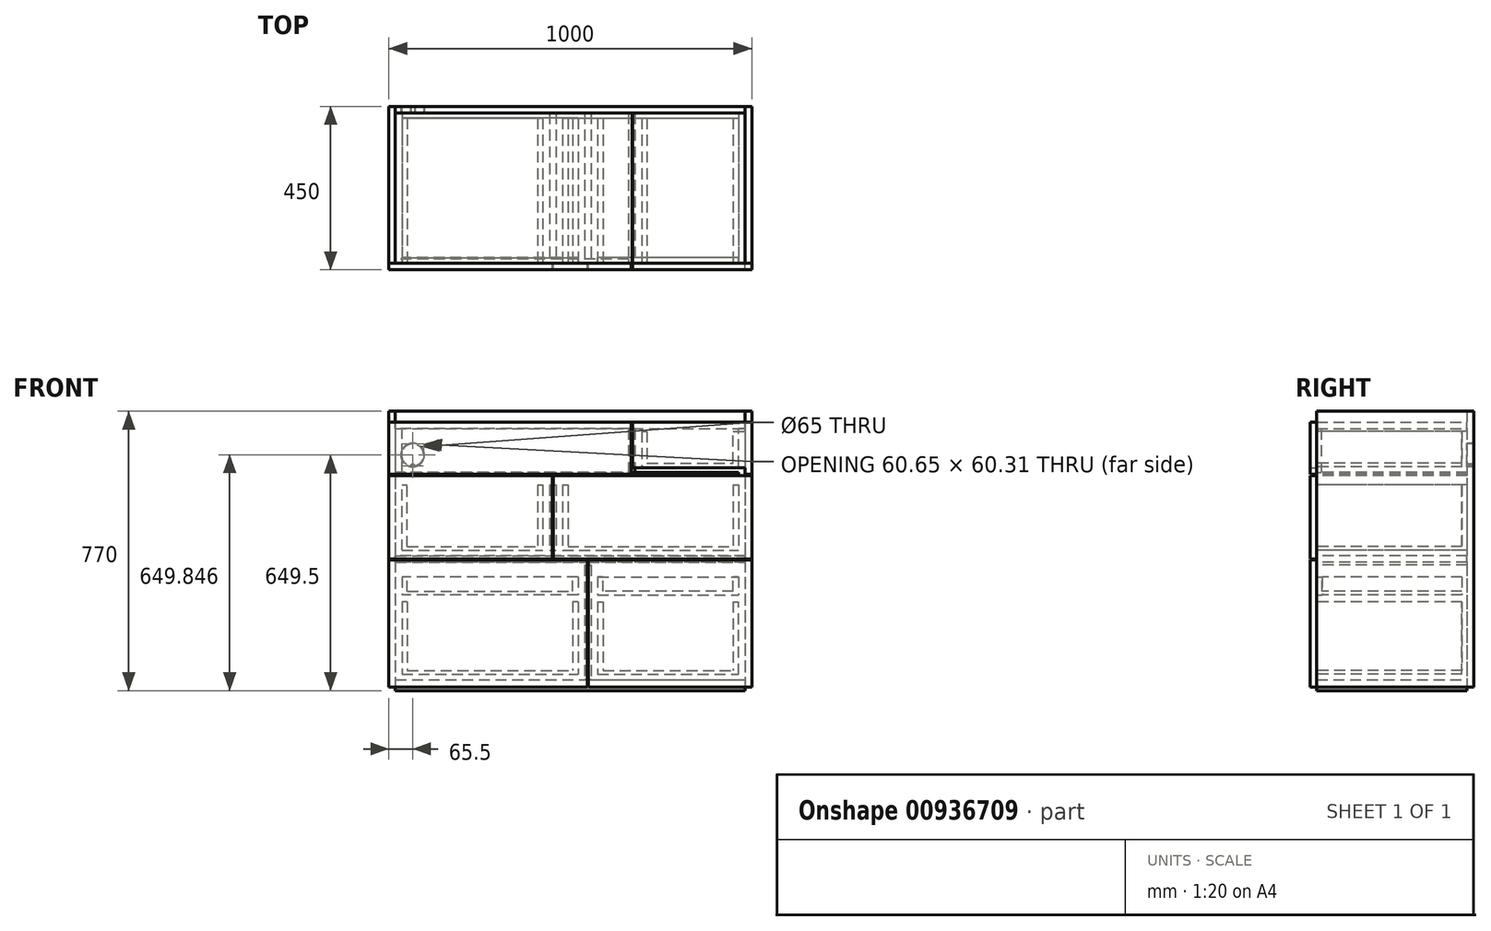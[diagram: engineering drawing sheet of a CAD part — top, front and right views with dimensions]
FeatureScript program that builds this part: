
annotation { "Feature Type Name" : "Feature", "Feature Type Description" : "" }
export const myFeature = defineFeature(function(context is Context, id is Id, definition is map)
    precondition{}
    {
        {
            var Q0;
            Q0=qCreatedBy(makeId("Top.planeOp"),FACE);
            var sketch = newSketch(context, id + "F0", { "sketchPlane" : qUnion([Q0])});
            skLineSegment(sketch, "E0.bottom", {"start": v(0, 0) * mm, "end": v(1000, 0) * mm});
            skLineSegment(sketch, "E0.top", {"start": v(0, 432) * mm, "end": v(1000, 432) * mm});
            skLineSegment(sketch, "E0.left", {"start": v(0, 0) * mm, "end": v(0, 432) * mm});
            skLineSegment(sketch, "E0.right", {"start": v(1000, 0) * mm, "end": v(1000, 432) * mm});
            skLineSegment(sketch, "E1.0", {"start": v(18, 0) * mm, "end": v(18, 432) * mm});
            skLineSegment(sketch, "E2", {"start": v(500, 455.77) * mm, "end": v(500, 504.04) * mm, "construction": true});
            skPoint(sketch, "E2.startSnap0", {"position": v(500, 432) * mm});
            skLineSegment(sketch, "E3.MirrorCS", {"start": v(982, 0) * mm, "end": v(982, 432) * mm});
            skLineSegment(sketch, "E4", {"start": v(1025.2, 216) * mm, "end": v(1096.23, 216) * mm, "construction": true});
            skPoint(sketch, "E4.startSnap0", {"position": v(1000, 216) * mm});
            skLineSegment(sketch, "E5.0", {"start": v(0, 414) * mm, "end": v(1000, 414) * mm});
            skSolve(sketch);
        }
        {
            var Q0;
            {var subQ0=sQuery(id+"F0.wireOp",EDGE,"E0.left");var subQ1=sQuery(id+"F0.wireOp",EDGE,"E0.bottom");var subQ2=makeQuery(id+"F0.imprint","INTERSECT",VERTEX,{"derivedFrom":[subQ1,subQ0]});Q0=makeQuery(id+"F0.imprint","IMPRINT",FACE,{"disambiguationData":[TD([[makeQuery(id+"F0.imprint","IMPRINT",EDGE,{"disambiguationData":[TD([[subQ2,-1.0]])],"derivedFrom":subQ1}),1.0]])]});}
            var Q1;
            {var subQ0=sQuery(id+"F0.wireOp",EDGE,"E0.left");var subQ1=sQuery(id+"F0.wireOp",EDGE,"E0.top");var subQ2=makeQuery(id+"F0.imprint","INTERSECT",VERTEX,{"derivedFrom":[subQ1,subQ0]});Q1=makeQuery(id+"F0.imprint","IMPRINT",FACE,{"disambiguationData":[TD([[makeQuery(id+"F0.imprint","IMPRINT",EDGE,{"disambiguationData":[TD([[subQ2,-1.0]])],"derivedFrom":subQ1}),-1.0]])]});}
            var Q2;
            {var subQ0=sQuery(id+"F0.wireOp",EDGE,"E0.right");var subQ1=sQuery(id+"F0.wireOp",EDGE,"E0.bottom");var subQ2=makeQuery(id+"F0.imprint","INTERSECT",VERTEX,{"derivedFrom":[subQ1,subQ0]});Q2=makeQuery(id+"F0.imprint","IMPRINT",FACE,{"disambiguationData":[TD([[makeQuery(id+"F0.imprint","IMPRINT",EDGE,{"disambiguationData":[TD([[subQ2,1.0]])],"derivedFrom":subQ1}),1.0]])]});}
            var Q3;
            {var subQ0=sQuery(id+"F0.wireOp",EDGE,"E0.right");var subQ1=sQuery(id+"F0.wireOp",EDGE,"E0.top");var subQ2=makeQuery(id+"F0.imprint","INTERSECT",VERTEX,{"derivedFrom":[subQ1,subQ0]});Q3=makeQuery(id+"F0.imprint","IMPRINT",FACE,{"disambiguationData":[TD([[makeQuery(id+"F0.imprint","IMPRINT",EDGE,{"disambiguationData":[TD([[subQ2,1.0]])],"derivedFrom":subQ1}),-1.0]])]});}
            extrude(context, id + "F1", {"entities" : qUnion([Q0, Q1, Q2, Q3]), "depth" : 760 * mm, "offsetDistance" : 25 * mm});
        }
        {
            var Q0;
            {var subQ0=sQuery(id+"F0.wireOp",EDGE,"E1.0");var subQ1=sQuery(id+"F0.wireOp",EDGE,"E0.top");var subQ2=makeQuery(id+"F0.imprint","INTERSECT",VERTEX,{"derivedFrom":[subQ1,subQ0]});Q0=makeQuery(id+"F0.imprint","IMPRINT",FACE,{"disambiguationData":[TD([[makeQuery(id+"F0.imprint","IMPRINT",EDGE,{"disambiguationData":[TD([[subQ2,-1.0]])],"derivedFrom":subQ1}),-1.0]])]});}
            var Q1;
            Q1=makeQuery(id+"F1.opExtrude","CAP_FACE",FACE,{"disambiguationData":[OSD([sQuery(id+"F0.wireOp",EDGE,"E0.bottom"),sQuery(id+"F0.wireOp",EDGE,"E0.top"),sQuery(id+"F0.wireOp",EDGE,"E0.left"),sQuery(id+"F0.wireOp",EDGE,"E1.0")])],"isStart":false});
            extrude(context, id + "F2", {"entities" : qUnion([Q0]), "endBound" : BoundingType.UP_TO_SURFACE, "depth" : 25 * mm, "endBoundEntityFace" : qUnion([Q1]), "offsetDistance" : 25 * mm});
        }
        {
            var Q0;
            {var subQ0=sQuery(id+"F0.wireOp",EDGE,"E1.0");var subQ1=sQuery(id+"F0.wireOp",EDGE,"E0.bottom");var subQ2=makeQuery(id+"F0.imprint","INTERSECT",VERTEX,{"derivedFrom":[subQ1,subQ0]});Q0=makeQuery(id+"F0.imprint","IMPRINT",FACE,{"disambiguationData":[TD([[makeQuery(id+"F0.imprint","IMPRINT",EDGE,{"disambiguationData":[TD([[subQ2,-1.0]])],"derivedFrom":subQ1}),1.0]])]});}
            extrude(context, id + "F3", {"entities" : qUnion([Q0]), "depth" : 20 * mm, "offsetDistance" : 25 * mm, "hasSecondDirection" : true, "secondDirectionOppositeDirection" : true, "secondDirectionDepth" : 10 * mm});
        }
        {
            var Q0;
            Q0=makeQuery(id+"F1.opExtrude","CAP_FACE",FACE,{"disambiguationData":[OSD([sQuery(id+"F0.wireOp",EDGE,"E0.bottom"),sQuery(id+"F0.wireOp",EDGE,"E0.top"),sQuery(id+"F0.wireOp",EDGE,"E0.left"),sQuery(id+"F0.wireOp",EDGE,"E1.0")])],"isStart":false});
            var sketch = newSketch(context, id + "F4", { "sketchPlane" : qUnion([Q0])});
            skLineSegment(sketch, "E6.bottom", {"start": v(0, 432) * mm, "end": v(1000, 432) * mm});
            skLineSegment(sketch, "E6.top", {"start": v(0, 0) * mm, "end": v(1000, 0) * mm});
            skLineSegment(sketch, "E6.left", {"start": v(0, 432) * mm, "end": v(0, 0) * mm});
            skLineSegment(sketch, "E6.right", {"start": v(1000, 432) * mm, "end": v(1000, 0) * mm});
            skLineSegment(sketch, "E7.bottom", {"start": v(18, 0) * mm, "end": v(982, 0) * mm});
            skLineSegment(sketch, "E7.top", {"start": v(18, 414) * mm, "end": v(982, 414) * mm});
            skLineSegment(sketch, "E7.left", {"start": v(18, 0) * mm, "end": v(18, 414) * mm});
            skLineSegment(sketch, "E7.right", {"start": v(982, 0) * mm, "end": v(982, 414) * mm});
            skLineSegment(sketch, "E8", {"start": v(671, 414) * mm, "end": v(671, 0) * mm});
            skLineSegment(sketch, "E9", {"start": v(18, 300) * mm, "end": v(671, 300) * mm});
            skLineSegment(sketch, "E10", {"start": v(55.2, 414) * mm, "end": v(55.2, -186) * mm, "construction": true});
            skLineSegment(sketch, "E11", {"start": v(-81.86, 114) * mm, "end": v(55.2, 114) * mm, "construction": true});
            skLineSegment(sketch, "E12", {"start": v(55.2, 0) * mm, "end": v(-78.13, 0) * mm, "construction": true});
            skLineSegment(sketch, "E13", {"start": v(55.2, -186) * mm, "end": v(-68.9, -186) * mm, "construction": true});
            skLineSegment(sketch, "E14.0", {"start": v(670, 414) * mm, "end": v(670, 0) * mm});
            skSolve(sketch);
        }
        {
            var Q0;
            {var subQ0=sQuery(id+"F4.wireOp",EDGE,"E7.right");Q0=makeQuery(id+"F4.imprint","IMPRINT",FACE,{"disambiguationData":[TD([[makeQuery(id+"F4.imprint","IMPRINT",EDGE,{"derivedFrom":subQ0}),1.0]])]});}
            var Q1;
            {var subQ0=sQuery(id+"F4.wireOp",EDGE,"E7.left");var subQ5=sQuery(id+"F4.wireOp",EDGE,"E9");var subQ7=makeQuery(id+"F4.imprint","INTERSECT",VERTEX,{"derivedFrom":[subQ0,subQ5]});Q1=makeQuery(id+"F4.imprint","IMPRINT",FACE,{"disambiguationData":[TD([[makeQuery(id+"F4.imprint","IMPRINT",EDGE,{"disambiguationData":[TD([[subQ7,-1.0]])],"derivedFrom":subQ5}),1.0]])]});}
            var Q2;
            {var subQ0=sQuery(id+"F4.wireOp",EDGE,"E7.left");var subQ5=sQuery(id+"F4.wireOp",EDGE,"E9");var subQ6=makeQuery(id+"F4.imprint","INTERSECT",VERTEX,{"derivedFrom":[subQ0,subQ5]});Q2=makeQuery(id+"F4.imprint","IMPRINT",FACE,{"disambiguationData":[TD([[makeQuery(id+"F4.imprint","IMPRINT",EDGE,{"disambiguationData":[TD([[subQ6,-1.0]])],"derivedFrom":subQ5}),-1.0]])]});}
            extrude(context, id + "F5", {"entities" : qUnion([Q0, Q1, Q2]), "oppositeDirection" : true, "depth" : 18 * mm, "offsetDistance" : 25 * mm});
        }
        {
            var Q0;
            Q0=makeQuery(id+"FaU98XOoRjI6tdl_2.opExtrude","SWEPT_BODY",BODY,{"disambiguationData":[OSD([sQuery(id+"F4.wireOp",EDGE,"E7.bottom"),sQuery(id+"F4.wireOp",EDGE,"E7.top"),sQuery(id+"F4.wireOp",EDGE,"E7.left"),sQuery(id+"F4.wireOp",EDGE,"E8")])]});
            var Q1;
            Q1=makeQuery(id+"F5.opExtrude","SWEPT_BODY",BODY,{"disambiguationData":[OSD([sQuery(id+"F4.wireOp",EDGE,"E7.bottom"),sQuery(id+"F4.wireOp",EDGE,"E7.top"),sQuery(id+"F4.wireOp",EDGE,"E7.right"),sQuery(id+"F4.wireOp",EDGE,"E8")])]});
            var Q2;
            Q2=makeQuery(id+"F5.opExtrude","SWEPT_BODY",BODY,{"disambiguationData":[OSD([sQuery(id+"F4.wireOp",EDGE,"E7.bottom"),sQuery(id+"F4.wireOp",EDGE,"E7.top"),sQuery(id+"F4.wireOp",EDGE,"E7.left"),sQuery(id+"F4.wireOp",EDGE,"E14.0")])]});
            transform(context, id + "F6", {"entities" : qUnion([Q0, Q1, Q2]), "transformType" : TransformType.TRANSLATION_3D, "dx" : 0 * mm, "dy" : 0 * mm, "dz" : -30 * mm, "makeCopy" : false});
        }
        {
            var Q0;
            {var subQ0=sQuery(id+"F0.wireOp",EDGE,"E0.bottom");Q0=makeQuery(id+"F1.opExtrude","SWEPT_FACE",FACE,{"disambiguationData":[OSD([subQ0]),TDD([makeQuery(id+"F0.imprint","IMPRINT",EDGE,{"disambiguationData":[TD([[makeQuery(id+"F0.imprint","INTERSECT",VERTEX,{"derivedFrom":[subQ0,sQuery(id+"F0.wireOp",EDGE,"E0.left")]}),-1.0]])],"derivedFrom":subQ0})])]});}
            var sketch = newSketch(context, id + "F7", { "sketchPlane" : qUnion([Q0])});
            skLineSegment(sketch, "E15.bottom", {"start": v(0, 730) * mm, "end": v(668, 730) * mm});
            skLineSegment(sketch, "E15.top", {"start": v(0, 586) * mm, "end": v(668, 586) * mm});
            skLineSegment(sketch, "E15.left", {"start": v(0, 730) * mm, "end": v(0, 586) * mm});
            skLineSegment(sketch, "E15.right", {"start": v(668, 730) * mm, "end": v(668, 586) * mm});
            skLineSegment(sketch, "E16.bottom", {"start": v(1000, 583) * mm, "end": v(756, 583) * mm});
            skLineSegment(sketch, "E16.top", {"start": v(1000, 353) * mm, "end": v(756, 353) * mm});
            skLineSegment(sketch, "E16.left", {"start": v(1000, 583) * mm, "end": v(1000, 353) * mm});
            skLineSegment(sketch, "E16.right", {"start": v(756, 583) * mm, "end": v(756, 353) * mm});
            skLineSegment(sketch, "E17.bottom", {"start": v(753, 583) * mm, "end": v(453, 583) * mm});
            skLineSegment(sketch, "E17.top", {"start": v(753, 353) * mm, "end": v(453, 353) * mm});
            skLineSegment(sketch, "E17.left", {"start": v(753, 583) * mm, "end": v(753, 353) * mm});
            skLineSegment(sketch, "E17.right", {"start": v(453, 583) * mm, "end": v(453, 353) * mm});
            skLineSegment(sketch, "E18.bottom", {"start": v(450, 583) * mm, "end": v(0, 583) * mm});
            skLineSegment(sketch, "E18.top", {"start": v(450, 353) * mm, "end": v(0, 353) * mm});
            skLineSegment(sketch, "E18.left", {"start": v(450, 583) * mm, "end": v(450, 353) * mm});
            skLineSegment(sketch, "E18.right", {"start": v(0, 583) * mm, "end": v(0, 353) * mm});
            skLineSegment(sketch, "E19.bottom", {"start": v(671, 730) * mm, "end": v(1000, 730) * mm});
            skLineSegment(sketch, "E19.top", {"start": v(671, 586) * mm, "end": v(1000, 586) * mm});
            skLineSegment(sketch, "E19.left", {"start": v(671, 730) * mm, "end": v(671, 586) * mm});
            skLineSegment(sketch, "E19.right", {"start": v(1000, 730) * mm, "end": v(1000, 586) * mm});
            skLineSegment(sketch, "E20", {"start": v(668, 658) * mm, "end": v(671, 658) * mm, "construction": true});
            skLineSegment(sketch, "E21", {"start": v(1108.22, 586) * mm, "end": v(1108.22, 583) * mm, "construction": true});
            skLineSegment(sketch, "E22", {"start": v(756, 468) * mm, "end": v(753, 468) * mm, "construction": true});
            skLineSegment(sketch, "E23", {"start": v(453, 468) * mm, "end": v(450, 468) * mm, "construction": true});
            skLineSegment(sketch, "E24.bottom", {"start": v(0, 0) * mm, "end": v(244, 0) * mm});
            skLineSegment(sketch, "E24.top", {"start": v(0, 350) * mm, "end": v(244, 350) * mm});
            skLineSegment(sketch, "E24.left", {"start": v(0, 0) * mm, "end": v(0, 350) * mm});
            skLineSegment(sketch, "E24.right", {"start": v(244, 0) * mm, "end": v(244, 350) * mm});
            skLineSegment(sketch, "E25.bottom", {"start": v(247, 350) * mm, "end": v(547, 350) * mm});
            skLineSegment(sketch, "E25.top", {"start": v(247, 0) * mm, "end": v(547, 0) * mm});
            skLineSegment(sketch, "E25.left", {"start": v(247, 350) * mm, "end": v(247, 0) * mm});
            skLineSegment(sketch, "E25.right", {"start": v(547, 350) * mm, "end": v(547, 0) * mm});
            skLineSegment(sketch, "E26.bottom", {"start": v(550, 350) * mm, "end": v(1000, 350) * mm});
            skLineSegment(sketch, "E26.top", {"start": v(550, 0) * mm, "end": v(1000, 0) * mm});
            skLineSegment(sketch, "E26.left", {"start": v(550, 350) * mm, "end": v(550, 0) * mm});
            skLineSegment(sketch, "E26.right", {"start": v(1000, 350) * mm, "end": v(1000, 0) * mm});
            skLineSegment(sketch, "E27", {"start": v(122, 353) * mm, "end": v(122, 350) * mm, "construction": true});
            skPoint(sketch, "E27.startSnap0", {"position": v(122, 350) * mm});
            skLineSegment(sketch, "E28", {"start": v(244, 175) * mm, "end": v(247, 175) * mm, "construction": true});
            skLineSegment(sketch, "E29", {"start": v(550, 175) * mm, "end": v(547, 175) * mm, "construction": true});
            skLineSegment(sketch, "E30.bottom", {"start": v(671, 586) * mm, "end": v(982, 586) * mm});
            skLineSegment(sketch, "E30.top", {"start": v(671, 604) * mm, "end": v(982, 604) * mm});
            skLineSegment(sketch, "E30.left", {"start": v(671, 586) * mm, "end": v(671, 604) * mm});
            skLineSegment(sketch, "E30.right", {"start": v(982, 586) * mm, "end": v(982, 604) * mm});
            skLineSegment(sketch, "E31", {"start": v(668, 712) * mm, "end": v(0, 712) * mm});
            skLineSegment(sketch, "E32", {"start": v(450, 583) * mm, "end": v(453, 583) * mm});
            skLineSegment(sketch, "E33", {"start": v(450, 353) * mm, "end": v(453, 353) * mm});
            skLineSegment(sketch, "E34", {"start": v(547, 350) * mm, "end": v(550, 350) * mm});
            skLineSegment(sketch, "E35", {"start": v(547, 0) * mm, "end": v(550, 0) * mm});
            skLineSegment(sketch, "E36", {"start": v(753, 583) * mm, "end": v(756, 583) * mm});
            skLineSegment(sketch, "E37", {"start": v(753, 353) * mm, "end": v(756, 353) * mm});
            skLineSegment(sketch, "E38", {"start": v(244, 350) * mm, "end": v(247, 350) * mm});
            skLineSegment(sketch, "E39", {"start": v(244, 0) * mm, "end": v(247, 0) * mm});
            skLineSegment(sketch, "E40", {"start": v(0, 666) * mm, "end": v(668, 666) * mm});
            skLineSegment(sketch, "E41", {"start": v(668, 730) * mm, "end": v(671, 730) * mm});
            skLineSegment(sketch, "E42", {"start": v(668, 586) * mm, "end": v(671, 586) * mm});
            skSolve(sketch);
        }
        {
            var Q0;
            {var subQ0=sQuery(id+"F7.wireOp",EDGE,"E18.left");Q0=makeQuery(id+"F7.imprint","IMPRINT",FACE,{"disambiguationData":[TD([[makeQuery(id+"F7.imprint","IMPRINT",EDGE,{"derivedFrom":subQ0}),-1.0]])]});}
            var Q1;
            Q1=makeQuery(id+"F7.imprint","IMPRINT",FACE,{"disambiguationData":[TD([[makeQuery(id+"F7.imprint","IMPRINT",EDGE,{"derivedFrom":sQuery(id+"F7.wireOp",EDGE,"E17.bottom")}),1.0]])]});
            var Q2;
            Q2=makeQuery(id+"F7.imprint","IMPRINT",FACE,{"disambiguationData":[TD([[makeQuery(id+"F7.imprint","IMPRINT",EDGE,{"derivedFrom":sQuery(id+"F7.wireOp",EDGE,"E16.bottom")}),1.0]])]});
            var Q3;
            Q3=makeQuery(id+"F7.imprint","IMPRINT",FACE,{"disambiguationData":[TD([[makeQuery(id+"F7.imprint","IMPRINT",EDGE,{"derivedFrom":sQuery(id+"F7.wireOp",EDGE,"E26.bottom")}),-1.0]])]});
            var Q4;
            Q4=makeQuery(id+"F7.imprint","IMPRINT",FACE,{"disambiguationData":[TD([[makeQuery(id+"F7.imprint","IMPRINT",EDGE,{"derivedFrom":sQuery(id+"F7.wireOp",EDGE,"E25.bottom")}),-1.0]])]});
            var Q5;
            {var subQ3=sQuery(id+"F7.wireOp",EDGE,"E24.right");Q5=makeQuery(id+"F7.imprint","IMPRINT",FACE,{"disambiguationData":[TD([[makeQuery(id+"F7.imprint","IMPRINT",EDGE,{"derivedFrom":subQ3}),1.0]])]});}
            var Q6;
            {var subQ0=sQuery(id+"F7.wireOp",EDGE,"E18.right");Q6=makeQuery(id+"F7.imprint","IMPRINT",FACE,{"disambiguationData":[TD([[makeQuery(id+"F7.imprint","IMPRINT",EDGE,{"derivedFrom":subQ0}),1.0]])]});}
            var Q7;
            {var subQ0=sQuery(id+"F7.wireOp",EDGE,"E24.left");Q7=makeQuery(id+"F7.imprint","IMPRINT",FACE,{"disambiguationData":[TD([[makeQuery(id+"F7.imprint","IMPRINT",EDGE,{"derivedFrom":subQ0}),1.0]])]});}
            var Q8;
            {var subQ0=sQuery(id+"F7.wireOp",EDGE,"E15.right");var subQ1=sQuery(id+"F7.wireOp",EDGE,"E15.top");var subQ2=makeQuery(id+"F7.imprint","INTERSECT",VERTEX,{"derivedFrom":[subQ1,subQ0]});Q8=makeQuery(id+"F7.imprint","IMPRINT",FACE,{"disambiguationData":[TD([[makeQuery(id+"F7.imprint","IMPRINT",EDGE,{"disambiguationData":[TD([[subQ2,1.0]])],"derivedFrom":subQ0}),-1.0]])]});}
            var Q9;
            Q9=makeQuery(id+"F7.imprint","IMPRINT",FACE,{"disambiguationData":[TD([[makeQuery(id+"F7.imprint","IMPRINT",EDGE,{"derivedFrom":sQuery(id+"F7.wireOp",EDGE,"E24.right")}),-1.0]])]});
            var Q10;
            Q10=makeQuery(id+"F7.imprint","IMPRINT",FACE,{"disambiguationData":[TD([[makeQuery(id+"F7.imprint","IMPRINT",EDGE,{"derivedFrom":sQuery(id+"F7.wireOp",EDGE,"E16.right")}),-1.0]])]});
            var Q11;
            {var subQ0=sQuery(id+"F7.wireOp",EDGE,"E15.left");var subQ6=sQuery(id+"F7.wireOp",EDGE,"E40");var subQ8=makeQuery(id+"F7.imprint","INTERSECT",VERTEX,{"derivedFrom":[subQ0,subQ6]});Q11=makeQuery(id+"F7.imprint","IMPRINT",FACE,{"disambiguationData":[TD([[makeQuery(id+"F7.imprint","IMPRINT",EDGE,{"disambiguationData":[TD([[subQ8,-1.0]])],"derivedFrom":subQ6}),-1.0]])]});}
            var Q12;
            {var subQ0=sQuery(id+"F7.wireOp",EDGE,"E31");var subQ1=sQuery(id+"F7.wireOp",EDGE,"E15.left");var subQ2=makeQuery(id+"F7.imprint","INTERSECT",VERTEX,{"derivedFrom":[subQ1,subQ0]});Q12=makeQuery(id+"F7.imprint","IMPRINT",FACE,{"disambiguationData":[TD([[makeQuery(id+"F7.imprint","IMPRINT",EDGE,{"disambiguationData":[TD([[subQ2,-1.0]])],"derivedFrom":subQ1}),1.0]])]});}
            var Q13;
            {var subQ0=sQuery(id+"F7.wireOp",EDGE,"E31");var subQ1=sQuery(id+"F7.wireOp",EDGE,"E15.right");var subQ2=makeQuery(id+"F7.imprint","INTERSECT",VERTEX,{"derivedFrom":[subQ1,subQ0]});Q13=makeQuery(id+"F7.imprint","IMPRINT",FACE,{"disambiguationData":[TD([[makeQuery(id+"F7.imprint","IMPRINT",EDGE,{"disambiguationData":[TD([[subQ2,-1.0]])],"derivedFrom":subQ1}),-1.0]])]});}
            var Q14;
            {var subQ0=sQuery(id+"F7.wireOp",EDGE,"E15.right");var subQ1=sQuery(id+"F7.wireOp",EDGE,"E15.bottom");var subQ2=makeQuery(id+"F7.imprint","INTERSECT",VERTEX,{"derivedFrom":[subQ1,subQ0]});Q14=makeQuery(id+"F7.imprint","IMPRINT",FACE,{"disambiguationData":[TD([[makeQuery(id+"F7.imprint","IMPRINT",EDGE,{"disambiguationData":[TD([[subQ2,-1.0]])],"derivedFrom":subQ0}),-1.0]])]});}
            var Q15;
            {var subQ0=sQuery(id+"F7.wireOp",EDGE,"E15.left");var subQ6=sQuery(id+"F7.wireOp",EDGE,"E31");var subQ7=makeQuery(id+"F7.imprint","INTERSECT",VERTEX,{"derivedFrom":[subQ0,subQ6]});Q15=makeQuery(id+"F7.imprint","IMPRINT",FACE,{"disambiguationData":[TD([[makeQuery(id+"F7.imprint","IMPRINT",EDGE,{"disambiguationData":[TD([[subQ7,1.0]])],"derivedFrom":subQ6}),-1.0]])]});}
            var Q16;
            Q16=makeQuery(id+"F7.imprint","IMPRINT",FACE,{"disambiguationData":[TD([[makeQuery(id+"F7.imprint","IMPRINT",EDGE,{"derivedFrom":sQuery(id+"F7.wireOp",EDGE,"E19.bottom")}),-1.0]])]});
            var Q17;
            Q17=makeQuery(id+"F7.imprint","IMPRINT",FACE,{"disambiguationData":[TD([[makeQuery(id+"F7.imprint","IMPRINT",EDGE,{"derivedFrom":sQuery(id+"F7.wireOp",EDGE,"E30.bottom")}),1.0]])]});
            extrude(context, id + "F8", {"entities" : qUnion([Q0, Q1, Q2, Q3, Q4, Q5, Q6, Q7, Q8, Q9, Q10, Q11, Q12, Q13, Q14, Q15, Q16, Q17]), "depth" : 18 * mm, "offsetDistance" : 25 * mm});
        }
        {
            var Q0;
            Q0=makeQuery(id+"F8.opExtrude","CAP_FACE",FACE,{"disambiguationData":[OSD([sQuery(id+"F7.wireOp",EDGE,"E15.bottom"),sQuery(id+"F7.wireOp",EDGE,"E15.top"),sQuery(id+"F7.wireOp",EDGE,"E15.left"),sQuery(id+"F7.wireOp",EDGE,"E15.right")])],"isStart":true});
            var sketch = newSketch(context, id + "F9", { "sketchPlane" : qUnion([Q0])});
            skLineSegment(sketch, "E43.bottom", {"start": v(-18, 583) * mm, "end": v(-982, 583) * mm});
            skLineSegment(sketch, "E43.top", {"start": v(-18, 565) * mm, "end": v(-982, 565) * mm});
            skLineSegment(sketch, "E43.left", {"start": v(-18, 583) * mm, "end": v(-18, 565) * mm});
            skLineSegment(sketch, "E43.right", {"start": v(-982, 583) * mm, "end": v(-982, 565) * mm});
            skLineSegment(sketch, "E44.bottom", {"start": v(-18, 361.75) * mm, "end": v(-982, 361.75) * mm});
            skLineSegment(sketch, "E44.top", {"start": v(-18, 343.75) * mm, "end": v(-982, 343.75) * mm});
            skLineSegment(sketch, "E44.left", {"start": v(-18, 361.75) * mm, "end": v(-18, 343.75) * mm});
            skLineSegment(sketch, "E44.right", {"start": v(-982, 361.75) * mm, "end": v(-982, 343.75) * mm});
            skLineSegment(sketch, "E45.bottom", {"start": v(-982, 565) * mm, "end": v(-964, 565) * mm});
            skLineSegment(sketch, "E45.top", {"start": v(-982, 361.75) * mm, "end": v(-964, 361.75) * mm});
            skLineSegment(sketch, "E45.left", {"start": v(-982, 565) * mm, "end": v(-982, 361.75) * mm});
            skLineSegment(sketch, "E45.right", {"start": v(-964, 565) * mm, "end": v(-964, 361.75) * mm});
            skLineSegment(sketch, "E46.bottom", {"start": v(-460.5, 565) * mm, "end": v(-442.5, 565) * mm});
            skLineSegment(sketch, "E46.top", {"start": v(-460.5, 361.75) * mm, "end": v(-442.5, 361.75) * mm});
            skLineSegment(sketch, "E46.left", {"start": v(-460.5, 565) * mm, "end": v(-460.5, 361.75) * mm});
            skLineSegment(sketch, "E46.right", {"start": v(-442.5, 565) * mm, "end": v(-442.5, 361.75) * mm});
            skLineSegment(sketch, "E47.bottom", {"start": v(-557.18, 343.75) * mm, "end": v(-539.18, 343.75) * mm});
            skLineSegment(sketch, "E47.top", {"start": v(-557.18, 20) * mm, "end": v(-539.18, 20) * mm});
            skLineSegment(sketch, "E47.left", {"start": v(-557.18, 343.75) * mm, "end": v(-557.18, 20) * mm});
            skLineSegment(sketch, "E47.right", {"start": v(-539.18, 343.75) * mm, "end": v(-539.18, 20) * mm});
            skLineSegment(sketch, "E48.bottom", {"start": v(-36, 343.75) * mm, "end": v(-18, 343.75) * mm});
            skLineSegment(sketch, "E48.top", {"start": v(-36, 20) * mm, "end": v(-18, 20) * mm});
            skLineSegment(sketch, "E48.left", {"start": v(-36, 343.75) * mm, "end": v(-36, 20) * mm});
            skLineSegment(sketch, "E48.right", {"start": v(-18, 343.75) * mm, "end": v(-18, 20) * mm});
            skLineSegment(sketch, "E49", {"start": v(-548.18, 289.25) * mm, "end": v(-548.18, 277.23) * mm, "construction": true});
            skPoint(sketch, "E50", {"position": v(-548.18, 20) * mm});
            skPoint(sketch, "E51", {"position": v(-27, 20) * mm});
            skPoint(sketch, "E52", {"position": v(-973, 361.75) * mm});
            skPoint(sketch, "E53", {"position": v(-451.5, 361.75) * mm});
            skLineSegment(sketch, "E54.bottom", {"start": v(-678.4, 712) * mm, "end": v(-660.4, 712) * mm});
            skLineSegment(sketch, "E54.left", {"start": v(-678.4, 712) * mm, "end": v(-678.4, 583) * mm});
            skLineSegment(sketch, "E54.right", {"start": v(-660.4, 712) * mm, "end": v(-660.4, 583) * mm});
            skLineSegment(sketch, "E55.bottom", {"start": v(-982, 583) * mm, "end": v(-964, 583) * mm});
            skLineSegment(sketch, "E55.top", {"start": v(-982, 712) * mm, "end": v(-964, 712) * mm});
            skLineSegment(sketch, "E55.left", {"start": v(-982, 583) * mm, "end": v(-982, 712) * mm});
            skLineSegment(sketch, "E55.right", {"start": v(-964, 583) * mm, "end": v(-964, 712) * mm});
            skLineSegment(sketch, "E56.bottom", {"start": v(-36, 361.75) * mm, "end": v(-51, 361.75) * mm});
            skLineSegment(sketch, "E56.top", {"start": v(-36, 565) * mm, "end": v(-51, 565) * mm});
            skLineSegment(sketch, "E56.left", {"start": v(-36, 361.75) * mm, "end": v(-36, 565) * mm});
            skLineSegment(sketch, "E56.right", {"start": v(-51, 361.75) * mm, "end": v(-51, 565) * mm});
            skLineSegment(sketch, "E57.0", {"start": v(-949, 557.5) * mm, "end": v(-949, 376.75) * mm});
            skLineSegment(sketch, "E58.0", {"start": v(-478.5, 557.5) * mm, "end": v(-478.5, 376.75) * mm});
            skLineSegment(sketch, "E59.0", {"start": v(-424.5, 580.07) * mm, "end": v(-424.5, 376.75) * mm});
            skLineSegment(sketch, "E60", {"start": v(-949, 343.75) * mm, "end": v(-949, 20) * mm});
            skLineSegment(sketch, "E61", {"start": v(-51, 343.75) * mm, "end": v(-51, 20) * mm});
            skLineSegment(sketch, "E62", {"start": v(-36, 35) * mm, "end": v(-949, 35) * mm});
            skLineSegment(sketch, "E63.0", {"start": v(-36, 45) * mm, "end": v(-949, 45) * mm});
            skLineSegment(sketch, "E64.0", {"start": v(-36, 376.75) * mm, "end": v(-964, 376.75) * mm});
            skLineSegment(sketch, "E65", {"start": v(-949, 35) * mm, "end": v(-964, 35) * mm});
            skLineSegment(sketch, "E66", {"start": v(-964, 35) * mm, "end": v(-964, 343.75) * mm});
            skLineSegment(sketch, "E67", {"start": v(-949, 45) * mm, "end": v(-964, 45) * mm});
            skLineSegment(sketch, "E68.0", {"start": v(-521.18, 343.75) * mm, "end": v(-521.18, 35) * mm});
            skLineSegment(sketch, "E69.0", {"start": v(-575.18, 343.75) * mm, "end": v(-575.18, 35) * mm});
            skLineSegment(sketch, "E70.0", {"start": v(-409.5, 580.07) * mm, "end": v(-409.5, 376.75) * mm});
            skLineSegment(sketch, "E71.0", {"start": v(-493.5, 557.5) * mm, "end": v(-493.5, 376.75) * mm});
            skLineSegment(sketch, "E72.0", {"start": v(-506.18, 343.75) * mm, "end": v(-506.18, 35) * mm});
            skLineSegment(sketch, "E73.0", {"start": v(-590.18, 343.75) * mm, "end": v(-590.18, 35) * mm});
            skLineSegment(sketch, "E74.0", {"start": v(-18, 336.25) * mm, "end": v(-982, 336.25) * mm});
            skLineSegment(sketch, "E75.0", {"start": v(-18, 557.5) * mm, "end": v(-982, 557.5) * mm});
            skLineSegment(sketch, "E76.0", {"start": v(-36, 386.75) * mm, "end": v(-964, 386.75) * mm});
            skLineSegment(sketch, "E77.top", {"start": v(118.2, 343.75) * mm, "end": v(882.2, 343.75) * mm});
            skLineSegment(sketch, "E77.left", {"start": v(118.2, 361.75) * mm, "end": v(118.2, 343.75) * mm});
            skLineSegment(sketch, "E77.right", {"start": v(882.2, 361.75) * mm, "end": v(882.2, 343.75) * mm});
            skLineSegment(sketch, "E78.bottom", {"start": v(118.2, 343.75) * mm, "end": v(136.2, 343.75) * mm});
            skLineSegment(sketch, "E78.top", {"start": v(118.2, 20) * mm, "end": v(136.2, 20) * mm});
            skLineSegment(sketch, "E78.left", {"start": v(118.2, 343.75) * mm, "end": v(118.2, 20) * mm});
            skLineSegment(sketch, "E78.right", {"start": v(136.2, 343.75) * mm, "end": v(136.2, 20) * mm});
            skPoint(sketch, "E79", {"position": v(118.2, 352.75) * mm});
            skPoint(sketch, "E80", {"position": v(127.2, 343.75) * mm});
            skLineSegment(sketch, "E81.bottom", {"start": v(882.2, 343.75) * mm, "end": v(864.2, 343.75) * mm});
            skLineSegment(sketch, "E81.top", {"start": v(882.2, 20) * mm, "end": v(864.2, 20) * mm});
            skLineSegment(sketch, "E81.left", {"start": v(882.2, 343.75) * mm, "end": v(882.2, 20) * mm});
            skLineSegment(sketch, "E81.right", {"start": v(864.2, 343.75) * mm, "end": v(864.2, 20) * mm});
            skLineSegment(sketch, "E82.bottom", {"start": v(864.2, 35) * mm, "end": v(136.2, 35) * mm});
            skLineSegment(sketch, "E82.top", {"start": v(864.2, 45) * mm, "end": v(136.2, 45) * mm});
            skLineSegment(sketch, "E82.left", {"start": v(864.2, 35) * mm, "end": v(864.2, 45) * mm});
            skLineSegment(sketch, "E82.right", {"start": v(136.2, 35) * mm, "end": v(136.2, 45) * mm});
            skLineSegment(sketch, "E83", {"start": v(864.2, 35) * mm, "end": v(882.2, 35) * mm});
            skLineSegment(sketch, "E84", {"start": v(136.2, 35) * mm, "end": v(118.2, 35) * mm});
            skLineSegment(sketch, "E85", {"start": v(361.6, 35) * mm, "end": v(361.6, 20) * mm, "construction": true});
            skLineSegment(sketch, "E86.bottom", {"start": v(882.2, 303.75) * mm, "end": v(136.2, 303.75) * mm});
            skLineSegment(sketch, "E86.top", {"start": v(882.2, 253.75) * mm, "end": v(136.2, 253.75) * mm});
            skLineSegment(sketch, "E86.left", {"start": v(882.2, 303.75) * mm, "end": v(882.2, 253.75) * mm});
            skLineSegment(sketch, "E86.right", {"start": v(136.2, 303.75) * mm, "end": v(136.2, 253.75) * mm});
            skLineSegment(sketch, "E87.0", {"start": v(849.2, 342.5) * mm, "end": v(849.2, 20) * mm});
            skLineSegment(sketch, "E88.0", {"start": v(151.2, 342.5) * mm, "end": v(151.2, 20) * mm});
            skLineSegment(sketch, "E89", {"start": v(136.2, 235) * mm, "end": v(151.2, 235) * mm});
            skLineSegment(sketch, "E90", {"start": v(849.2, 235) * mm, "end": v(864.2, 235) * mm});
            skLineSegment(sketch, "E91.0", {"start": v(882.2, 263.75) * mm, "end": v(136.2, 263.75) * mm});
            skLineSegment(sketch, "E92", {"start": v(-521.18, 253.75) * mm, "end": v(-36, 253.75) * mm});
            skLineSegment(sketch, "E93.0", {"start": v(-521.18, 263.75) * mm, "end": v(-36, 263.75) * mm});
            skLineSegment(sketch, "E94.0", {"start": v(-521.18, 303.75) * mm, "end": v(-36, 303.75) * mm});
            skLineSegment(sketch, "E95", {"start": v(-521.18, 235) * mm, "end": v(-506.18, 235) * mm});
            skLineSegment(sketch, "E96", {"start": v(-51, 235) * mm, "end": v(-36, 235) * mm});
            skLineSegment(sketch, "E97", {"start": v(-575.18, 253.75) * mm, "end": v(-964, 253.75) * mm});
            skLineSegment(sketch, "E98", {"start": v(-575.18, 263.75) * mm, "end": v(-964, 263.75) * mm});
            skLineSegment(sketch, "E99", {"start": v(-575.18, 303.75) * mm, "end": v(-964, 303.75) * mm});
            skLineSegment(sketch, "E100", {"start": v(-575.18, 235) * mm, "end": v(-590.18, 235) * mm});
            skLineSegment(sketch, "E101", {"start": v(-949, 235) * mm, "end": v(-964, 235) * mm});
            skLineSegment(sketch, "E102", {"start": v(-668, 592) * mm, "end": v(-982, 592) * mm});
            skLineSegment(sketch, "E103.bottom", {"start": v(-18, 583) * mm, "end": v(-36, 583) * mm});
            skLineSegment(sketch, "E103.top", {"start": v(-18, 712) * mm, "end": v(-36, 712) * mm});
            skLineSegment(sketch, "E103.left", {"start": v(-18, 583) * mm, "end": v(-18, 712) * mm});
            skLineSegment(sketch, "E103.right", {"start": v(-36, 583) * mm, "end": v(-36, 712) * mm});
            skLineSegment(sketch, "E104.0", {"start": v(-18, 574) * mm, "end": v(-982, 574) * mm});
            skLineSegment(sketch, "E105", {"start": v(-668, 592) * mm, "end": v(-18, 592) * mm});
            skPoint(sketch, "E106", {"position": v(-669.4, 712) * mm});
            skLineSegment(sketch, "E107.0", {"start": v(-949, 583) * mm, "end": v(-949, 712) * mm});
            skLineSegment(sketch, "E108.0", {"start": v(-696.4, 712) * mm, "end": v(-696.4, 583) * mm});
            skLineSegment(sketch, "E109.0", {"start": v(-668, 607) * mm, "end": v(-982, 607) * mm});
            skLineSegment(sketch, "E110.0", {"start": v(-671, 704.5) * mm, "end": v(-982, 704.5) * mm});
            skLineSegment(sketch, "E111.0", {"start": v(-668, 617) * mm, "end": v(-982, 617) * mm});
            skLineSegment(sketch, "E112.0", {"start": v(-711.4, 712) * mm, "end": v(-711.4, 583) * mm});
            skSolve(sketch);
        }
        {
            var Q0;
            {var subQ2=sQuery(id+"F9.wireOp",EDGE,"E44.left");Q0=makeQuery(id+"F9.imprint","IMPRINT",FACE,{"disambiguationData":[TD([[makeQuery(id+"F9.imprint","IMPRINT",EDGE,{"derivedFrom":subQ2}),-1.0]])]});}
            var Q1;
            {var subQ4=sQuery(id+"F9.wireOp",EDGE,"E55.bottom");Q1=makeQuery(id+"F9.imprint","IMPRINT",FACE,{"disambiguationData":[TD([[makeQuery(id+"F9.imprint","IMPRINT",EDGE,{"derivedFrom":subQ4}),-1.0]])]});}
            var Q2;
            {var subQ1=sQuery(id+"F9.wireOp",EDGE,"E43.bottom");var subQ3=sQuery(id+"F9.wireOp",EDGE,"E54.left");var subQ4=makeQuery(id+"F9.imprint","INTERSECT",VERTEX,{"derivedFrom":[subQ1,subQ3]});Q2=makeQuery(id+"F9.imprint","IMPRINT",FACE,{"disambiguationData":[TD([[makeQuery(id+"F9.imprint","IMPRINT",EDGE,{"disambiguationData":[TD([[subQ4,1.0]])],"derivedFrom":subQ3}),-1.0]])]});}
            var Q3;
            {var subQ2=sQuery(id+"F9.wireOp",EDGE,"E43.bottom");var subQ4=sQuery(id+"F9.wireOp",EDGE,"E54.left");var subQ5=makeQuery(id+"F9.imprint","INTERSECT",VERTEX,{"derivedFrom":[subQ2,subQ4]});Q3=makeQuery(id+"F9.imprint","IMPRINT",FACE,{"disambiguationData":[TD([[makeQuery(id+"F9.imprint","IMPRINT",EDGE,{"disambiguationData":[TD([[subQ5,1.0]])],"derivedFrom":subQ2}),-1.0]])]});}
            var Q4;
            {var subQ0=sQuery(id+"F9.wireOp",EDGE,"E55.bottom");Q4=makeQuery(id+"F9.imprint","IMPRINT",FACE,{"disambiguationData":[TD([[makeQuery(id+"F9.imprint","IMPRINT",EDGE,{"derivedFrom":subQ0}),1.0]])]});}
            var Q5;
            {var subQ3=sQuery(id+"F9.wireOp",EDGE,"E105");var subQ5=sQuery(id+"F9.wireOp",EDGE,"E103.right");var subQ6=makeQuery(id+"F9.imprint","INTERSECT",VERTEX,{"derivedFrom":[subQ5,subQ3]});Q5=makeQuery(id+"F9.imprint","IMPRINT",FACE,{"disambiguationData":[TD([[makeQuery(id+"F9.imprint","IMPRINT",EDGE,{"disambiguationData":[TD([[subQ6,1.0]])],"derivedFrom":subQ5}),1.0]])]});}
            var Q6;
            {var subQ0=sQuery(id+"F9.wireOp",EDGE,"E105");var subQ1=sQuery(id+"F9.wireOp",EDGE,"E103.left");var subQ2=makeQuery(id+"F9.imprint","INTERSECT",VERTEX,{"derivedFrom":[subQ1,subQ0]});Q6=makeQuery(id+"F9.imprint","IMPRINT",FACE,{"disambiguationData":[TD([[makeQuery(id+"F9.imprint","IMPRINT",EDGE,{"disambiguationData":[TD([[subQ2,1.0]])],"derivedFrom":subQ1}),1.0]])]});}
            var Q7;
            {var subQ0=sQuery(id+"F9.wireOp",EDGE,"E103.bottom");Q7=makeQuery(id+"F9.imprint","IMPRINT",FACE,{"disambiguationData":[TD([[makeQuery(id+"F9.imprint","IMPRINT",EDGE,{"derivedFrom":subQ0}),-1.0]])]});}
            var Q8;
            {var subQ3=sQuery(id+"F9.wireOp",EDGE,"E54.right");var subQ5=makeQuery(id+"F8.opExtrude","CAP_EDGE",EDGE,{"disambiguationData":[OSD([sQuery(id+"F7.wireOp",EDGE,"E15.top")])],"isStart":true});var subQ6=makeQuery(id+"F9.imprint","INTERSECT",VERTEX,{"derivedFrom":[subQ5,subQ3]});Q8=makeQuery(id+"F9.imprint","IMPRINT",FACE,{"disambiguationData":[TD([[makeQuery(id+"F9.imprint","IMPRINT",EDGE,{"disambiguationData":[TD([[subQ6,-1.0]])],"derivedFrom":subQ3}),1.0]])]});}
            var Q9;
            {var subQ0=sQuery(id+"F9.wireOp",EDGE,"E105");var subQ1=sQuery(id+"F9.wireOp",EDGE,"E54.right");var subQ2=makeQuery(id+"F9.imprint","INTERSECT",VERTEX,{"derivedFrom":[subQ1,subQ0]});Q9=makeQuery(id+"F9.imprint","IMPRINT",FACE,{"disambiguationData":[TD([[makeQuery(id+"F9.imprint","IMPRINT",EDGE,{"disambiguationData":[TD([[subQ2,-1.0]])],"derivedFrom":subQ1}),-1.0]])]});}
            var Q10;
            {var subQ0=sQuery(id+"F9.wireOp",EDGE,"E107.0");var subQ1=sQuery(id+"F9.wireOp",EDGE,"E43.bottom");var subQ2=makeQuery(id+"F9.imprint","INTERSECT",VERTEX,{"derivedFrom":[subQ1,subQ0]});Q10=makeQuery(id+"F9.imprint","IMPRINT",FACE,{"disambiguationData":[TD([[makeQuery(id+"F9.imprint","IMPRINT",EDGE,{"disambiguationData":[TD([[subQ2,1.0]])],"derivedFrom":subQ1}),-1.0]])]});}
            var Q11;
            {var subQ0=sQuery(id+"F9.wireOp",EDGE,"E55.right");var subQ5=sQuery(id+"F9.wireOp",EDGE,"E102");var subQ6=makeQuery(id+"F9.imprint","INTERSECT",VERTEX,{"derivedFrom":[subQ0,subQ5]});Q11=makeQuery(id+"F9.imprint","IMPRINT",FACE,{"disambiguationData":[TD([[makeQuery(id+"F9.imprint","IMPRINT",EDGE,{"disambiguationData":[TD([[subQ6,1.0]])],"derivedFrom":subQ5}),1.0]])]});}
            var Q12;
            {var subQ0=sQuery(id+"F9.wireOp",EDGE,"E108.0");var subQ1=sQuery(id+"F9.wireOp",EDGE,"E43.bottom");var subQ2=makeQuery(id+"F9.imprint","INTERSECT",VERTEX,{"derivedFrom":[subQ1,subQ0]});Q12=makeQuery(id+"F9.imprint","IMPRINT",FACE,{"disambiguationData":[TD([[makeQuery(id+"F9.imprint","IMPRINT",EDGE,{"disambiguationData":[TD([[subQ2,-1.0]])],"derivedFrom":subQ1}),-1.0]])]});}
            var Q13;
            Q13=makeQuery(id+"F5.opExtrude","SWEPT_FACE",FACE,{"disambiguationData":[OSD([sQuery(id+"F4.wireOp",EDGE,"E7.top")])]});
            extrude(context, id + "F10", {"entities" : qUnion([Q0, Q1, Q2, Q3, Q4, Q5, Q6, Q7, Q8, Q9, Q10, Q11, Q12]), "endBound" : BoundingType.UP_TO_SURFACE, "depth" : 25 * mm, "endBoundEntityFace" : qUnion([Q13]), "offsetDistance" : 25 * mm});
        }
        {
            var Q0;
            Q0=makeQuery(id+"F9.imprint","IMPRINT",FACE,{"disambiguationData":[TD([[makeQuery(id+"F9.imprint","IMPRINT",EDGE,{"derivedFrom":sQuery(id+"F9.wireOp",EDGE,"E54.bottom")}),-1.0]])]});
            var Q1;
            Q1=makeQuery(id+"F9.imprint","IMPRINT",FACE,{"disambiguationData":[TD([[makeQuery(id+"F9.imprint","IMPRINT",EDGE,{"derivedFrom":sQuery(id+"F9.wireOp",EDGE,"E46.bottom")}),-1.0]])]});
            var Q2;
            Q2=makeQuery(id+"F9.imprint","IMPRINT",FACE,{"disambiguationData":[TD([[makeQuery(id+"F9.imprint","IMPRINT",EDGE,{"derivedFrom":sQuery(id+"F9.wireOp",EDGE,"E47.bottom")}),-1.0]])]});
            var Q3;
            {var subQ0=sQuery(id+"F9.wireOp",EDGE,"E75.0");var subQ1=sQuery(id+"F9.wireOp",EDGE,"E46.left");var subQ2=makeQuery(id+"F9.imprint","INTERSECT",VERTEX,{"derivedFrom":[subQ1,subQ0]});Q3=makeQuery(id+"F9.imprint","IMPRINT",FACE,{"disambiguationData":[TD([[makeQuery(id+"F9.imprint","IMPRINT",EDGE,{"disambiguationData":[TD([[subQ2,-1.0]])],"derivedFrom":subQ1}),1.0]])]});}
            var Q4;
            {var subQ0=sQuery(id+"F9.wireOp",EDGE,"E76.0");var subQ1=sQuery(id+"F9.wireOp",EDGE,"E46.left");var subQ2=makeQuery(id+"F9.imprint","INTERSECT",VERTEX,{"derivedFrom":[subQ1,subQ0]});Q4=makeQuery(id+"F9.imprint","IMPRINT",FACE,{"disambiguationData":[TD([[makeQuery(id+"F9.imprint","IMPRINT",EDGE,{"disambiguationData":[TD([[subQ2,-1.0]])],"derivedFrom":subQ1}),1.0]])]});}
            var Q5;
            {var subQ0=sQuery(id+"F9.wireOp",EDGE,"E46.top");Q5=makeQuery(id+"F9.imprint","IMPRINT",FACE,{"disambiguationData":[TD([[makeQuery(id+"F9.imprint","IMPRINT",EDGE,{"derivedFrom":subQ0}),1.0]])]});}
            var Q6;
            {var subQ0=sQuery(id+"F9.wireOp",EDGE,"E74.0");var subQ1=sQuery(id+"F9.wireOp",EDGE,"E47.left");var subQ2=makeQuery(id+"F9.imprint","INTERSECT",VERTEX,{"derivedFrom":[subQ1,subQ0]});Q6=makeQuery(id+"F9.imprint","IMPRINT",FACE,{"disambiguationData":[TD([[makeQuery(id+"F9.imprint","IMPRINT",EDGE,{"disambiguationData":[TD([[subQ2,-1.0]])],"derivedFrom":subQ1}),1.0]])]});}
            var Q7;
            {var subQ0=sQuery(id+"F9.wireOp",EDGE,"E62");var subQ1=sQuery(id+"F9.wireOp",EDGE,"E47.left");var subQ2=makeQuery(id+"F9.imprint","INTERSECT",VERTEX,{"derivedFrom":[subQ1,subQ0]});Q7=makeQuery(id+"F9.imprint","IMPRINT",FACE,{"disambiguationData":[TD([[makeQuery(id+"F9.imprint","IMPRINT",EDGE,{"disambiguationData":[TD([[subQ2,1.0]])],"derivedFrom":subQ1}),1.0]])]});}
            var Q8;
            {var subQ0=sQuery(id+"F9.wireOp",EDGE,"E47.top");Q8=makeQuery(id+"F9.imprint","IMPRINT",FACE,{"disambiguationData":[TD([[makeQuery(id+"F9.imprint","IMPRINT",EDGE,{"derivedFrom":subQ0}),1.0]])]});}
            var Q9;
            {var subQ0=sQuery(id+"F9.wireOp",EDGE,"E55.top");Q9=makeQuery(id+"F9.imprint","IMPRINT",FACE,{"disambiguationData":[TD([[makeQuery(id+"F9.imprint","IMPRINT",EDGE,{"derivedFrom":subQ0}),-1.0]])]});}
            var Q10;
            {var subQ0=sQuery(id+"F9.wireOp",EDGE,"E103.top");Q10=makeQuery(id+"F9.imprint","IMPRINT",FACE,{"disambiguationData":[TD([[makeQuery(id+"F9.imprint","IMPRINT",EDGE,{"derivedFrom":subQ0}),1.0]])]});}
            var Q11;
            {var subQ0=sQuery(id+"F9.wireOp",EDGE,"E105");var subQ1=sQuery(id+"F9.wireOp",EDGE,"E103.left");var subQ2=makeQuery(id+"F9.imprint","INTERSECT",VERTEX,{"derivedFrom":[subQ1,subQ0]});Q11=makeQuery(id+"F9.imprint","IMPRINT",FACE,{"disambiguationData":[TD([[makeQuery(id+"F9.imprint","IMPRINT",EDGE,{"disambiguationData":[TD([[subQ2,-1.0]])],"derivedFrom":subQ1}),1.0]])]});}
            var Q12;
            {var subQ0=sQuery(id+"F9.wireOp",EDGE,"E109.0");var subQ1=sQuery(id+"F9.wireOp",EDGE,"E54.left");var subQ2=makeQuery(id+"F9.imprint","INTERSECT",VERTEX,{"derivedFrom":[subQ1,subQ0]});Q12=makeQuery(id+"F9.imprint","IMPRINT",FACE,{"disambiguationData":[TD([[makeQuery(id+"F9.imprint","IMPRINT",EDGE,{"disambiguationData":[TD([[subQ2,-1.0]])],"derivedFrom":subQ1}),1.0]])]});}
            var Q13;
            {var subQ0=sQuery(id+"F9.wireOp",EDGE,"E111.0");var subQ1=sQuery(id+"F9.wireOp",EDGE,"E54.left");var subQ2=makeQuery(id+"F9.imprint","INTERSECT",VERTEX,{"derivedFrom":[subQ1,subQ0]});Q13=makeQuery(id+"F9.imprint","IMPRINT",FACE,{"disambiguationData":[TD([[makeQuery(id+"F9.imprint","IMPRINT",EDGE,{"disambiguationData":[TD([[subQ2,-1.0]])],"derivedFrom":subQ1}),1.0]])]});}
            var Q14;
            {var subQ4=sQuery(id+"F9.wireOp",EDGE,"E54.right");var subQ7=sQuery(id+"F9.wireOp",EDGE,"E54.bottom");var subQ9=makeQuery(id+"F9.imprint","INTERSECT",VERTEX,{"derivedFrom":[subQ7,subQ4]});Q14=makeQuery(id+"F9.imprint","IMPRINT",FACE,{"disambiguationData":[TD([[makeQuery(id+"F9.imprint","IMPRINT",EDGE,{"disambiguationData":[TD([[subQ9,1.0]])],"derivedFrom":subQ7}),-1.0]])]});}
            var Q15;
            Q15=makeQuery(id+"F3.opExtrude","SWEPT_FACE",FACE,{"disambiguationData":[OSD([sQuery(id+"F0.wireOp",EDGE,"E5.0")])]});
            extrude(context, id + "F11", {"entities" : qUnion([Q0, Q1, Q2, Q3, Q4, Q5, Q6, Q7, Q8, Q9, Q10, Q11, Q12, Q13, Q14]), "endBound" : BoundingType.UP_TO_SURFACE, "depth" : 25 * mm, "endBoundEntityFace" : qUnion([Q15]), "offsetDistance" : 25 * mm});
        }
        {
            var Q0;
            {var subQ0=sQuery(id+"F9.wireOp",EDGE,"E76.0");var subQ1=sQuery(id+"F9.wireOp",EDGE,"E56.left");var subQ2=makeQuery(id+"F9.imprint","INTERSECT",VERTEX,{"derivedFrom":[subQ1,subQ0]});Q0=makeQuery(id+"F9.imprint","IMPRINT",FACE,{"disambiguationData":[TD([[makeQuery(id+"F9.imprint","IMPRINT",EDGE,{"disambiguationData":[TD([[subQ2,-1.0]])],"derivedFrom":subQ1}),1.0]])]});}
            var Q1;
            {var subQ0=sQuery(id+"F9.wireOp",EDGE,"E64.0");var subQ1=sQuery(id+"F9.wireOp",EDGE,"E56.left");var subQ2=makeQuery(id+"F9.imprint","INTERSECT",VERTEX,{"derivedFrom":[subQ1,subQ0]});Q1=makeQuery(id+"F9.imprint","IMPRINT",FACE,{"disambiguationData":[TD([[makeQuery(id+"F9.imprint","IMPRINT",EDGE,{"disambiguationData":[TD([[subQ2,-1.0]])],"derivedFrom":subQ1}),1.0]])]});}
            var Q2;
            {var subQ0=sQuery(id+"F9.wireOp",EDGE,"E64.0");var subQ1=sQuery(id+"F9.wireOp",EDGE,"E56.right");var subQ2=makeQuery(id+"F9.imprint","INTERSECT",VERTEX,{"derivedFrom":[subQ1,subQ0]});Q2=makeQuery(id+"F9.imprint","IMPRINT",FACE,{"disambiguationData":[TD([[makeQuery(id+"F9.imprint","IMPRINT",EDGE,{"disambiguationData":[TD([[subQ2,-1.0]])],"derivedFrom":subQ1}),1.0]])]});}
            var Q3;
            {var subQ0=sQuery(id+"F9.wireOp",EDGE,"E76.0");var subQ1=sQuery(id+"F9.wireOp",EDGE,"E59.0");var subQ2=makeQuery(id+"F9.imprint","INTERSECT",VERTEX,{"derivedFrom":[subQ1,subQ0]});Q3=makeQuery(id+"F9.imprint","IMPRINT",FACE,{"disambiguationData":[TD([[makeQuery(id+"F9.imprint","IMPRINT",EDGE,{"disambiguationData":[TD([[subQ2,-1.0]])],"derivedFrom":subQ1}),1.0]])]});}
            var Q4;
            {var subQ0=sQuery(id+"F9.wireOp",EDGE,"E75.0");var subQ1=sQuery(id+"F9.wireOp",EDGE,"E59.0");var subQ2=makeQuery(id+"F9.imprint","INTERSECT",VERTEX,{"derivedFrom":[subQ1,subQ0]});Q4=makeQuery(id+"F9.imprint","IMPRINT",FACE,{"disambiguationData":[TD([[makeQuery(id+"F9.imprint","IMPRINT",EDGE,{"disambiguationData":[TD([[subQ2,-1.0]])],"derivedFrom":subQ1}),1.0]])]});}
            var Q5;
            {var subQ0=sQuery(id+"F9.wireOp",EDGE,"E75.0");var subQ1=sQuery(id+"F9.wireOp",EDGE,"E58.0");var subQ2=makeQuery(id+"F9.imprint","INTERSECT",VERTEX,{"derivedFrom":[subQ1,subQ0]});Q5=makeQuery(id+"F9.imprint","IMPRINT",FACE,{"disambiguationData":[TD([[makeQuery(id+"F9.imprint","IMPRINT",EDGE,{"disambiguationData":[TD([[subQ2,-1.0]])],"derivedFrom":subQ1}),-1.0]])]});}
            var Q6;
            {var subQ0=sQuery(id+"F9.wireOp",EDGE,"E76.0");var subQ1=sQuery(id+"F9.wireOp",EDGE,"E58.0");var subQ2=makeQuery(id+"F9.imprint","INTERSECT",VERTEX,{"derivedFrom":[subQ1,subQ0]});Q6=makeQuery(id+"F9.imprint","IMPRINT",FACE,{"disambiguationData":[TD([[makeQuery(id+"F9.imprint","IMPRINT",EDGE,{"disambiguationData":[TD([[subQ2,-1.0]])],"derivedFrom":subQ1}),-1.0]])]});}
            var Q7;
            {var subQ0=sQuery(id+"F9.wireOp",EDGE,"E76.0");var subQ1=sQuery(id+"F9.wireOp",EDGE,"E57.0");var subQ2=makeQuery(id+"F9.imprint","INTERSECT",VERTEX,{"derivedFrom":[subQ1,subQ0]});Q7=makeQuery(id+"F9.imprint","IMPRINT",FACE,{"disambiguationData":[TD([[makeQuery(id+"F9.imprint","IMPRINT",EDGE,{"disambiguationData":[TD([[subQ2,-1.0]])],"derivedFrom":subQ1}),1.0]])]});}
            var Q8;
            {var subQ0=sQuery(id+"F9.wireOp",EDGE,"E64.0");var subQ1=sQuery(id+"F9.wireOp",EDGE,"E45.right");var subQ2=makeQuery(id+"F9.imprint","INTERSECT",VERTEX,{"derivedFrom":[subQ1,subQ0]});Q8=makeQuery(id+"F9.imprint","IMPRINT",FACE,{"disambiguationData":[TD([[makeQuery(id+"F9.imprint","IMPRINT",EDGE,{"disambiguationData":[TD([[subQ2,1.0]])],"derivedFrom":subQ1}),1.0]])]});}
            var Q9;
            {var subQ0=sQuery(id+"F9.wireOp",EDGE,"E76.0");var subQ1=sQuery(id+"F9.wireOp",EDGE,"E45.right");var subQ2=makeQuery(id+"F9.imprint","INTERSECT",VERTEX,{"derivedFrom":[subQ1,subQ0]});Q9=makeQuery(id+"F9.imprint","IMPRINT",FACE,{"disambiguationData":[TD([[makeQuery(id+"F9.imprint","IMPRINT",EDGE,{"disambiguationData":[TD([[subQ2,1.0]])],"derivedFrom":subQ1}),1.0]])]});}
            var Q10;
            {var subQ0=sQuery(id+"F9.wireOp",EDGE,"E67");Q10=makeQuery(id+"F9.imprint","IMPRINT",FACE,{"disambiguationData":[TD([[makeQuery(id+"F9.imprint","IMPRINT",EDGE,{"derivedFrom":subQ0}),-1.0]])]});}
            var Q11;
            {var subQ0=sQuery(id+"F9.wireOp",EDGE,"E65");Q11=makeQuery(id+"F9.imprint","IMPRINT",FACE,{"disambiguationData":[TD([[makeQuery(id+"F9.imprint","IMPRINT",EDGE,{"derivedFrom":subQ0}),-1.0]])]});}
            var Q12;
            {var subQ0=sQuery(id+"F9.wireOp",EDGE,"E62");var subQ5=sQuery(id+"F9.wireOp",EDGE,"E73.0");var subQ6=makeQuery(id+"F9.imprint","INTERSECT",VERTEX,{"derivedFrom":[subQ0,subQ5]});Q12=makeQuery(id+"F9.imprint","IMPRINT",FACE,{"disambiguationData":[TD([[makeQuery(id+"F9.imprint","IMPRINT",EDGE,{"disambiguationData":[TD([[subQ6,1.0]])],"derivedFrom":subQ5}),-1.0]])]});}
            var Q13;
            {var subQ0=sQuery(id+"F9.wireOp",EDGE,"E69.0");var subQ1=sQuery(id+"F9.wireOp",EDGE,"E62");var subQ2=makeQuery(id+"F9.imprint","INTERSECT",VERTEX,{"derivedFrom":[subQ1,subQ0]});Q13=makeQuery(id+"F9.imprint","IMPRINT",FACE,{"disambiguationData":[TD([[makeQuery(id+"F9.imprint","IMPRINT",EDGE,{"disambiguationData":[TD([[subQ2,-1.0]])],"derivedFrom":subQ1}),-1.0]])]});}
            var Q14;
            {var subQ0=sQuery(id+"F9.wireOp",EDGE,"E69.0");var subQ1=sQuery(id+"F9.wireOp",EDGE,"E63.0");var subQ2=makeQuery(id+"F9.imprint","INTERSECT",VERTEX,{"derivedFrom":[subQ1,subQ0]});Q14=makeQuery(id+"F9.imprint","IMPRINT",FACE,{"disambiguationData":[TD([[makeQuery(id+"F9.imprint","IMPRINT",EDGE,{"disambiguationData":[TD([[subQ2,-1.0]])],"derivedFrom":subQ1}),-1.0]])]});}
            var Q15;
            {var subQ0=sQuery(id+"F9.wireOp",EDGE,"E72.0");var subQ1=sQuery(id+"F9.wireOp",EDGE,"E62");var subQ2=makeQuery(id+"F9.imprint","INTERSECT",VERTEX,{"derivedFrom":[subQ1,subQ0]});Q15=makeQuery(id+"F9.imprint","IMPRINT",FACE,{"disambiguationData":[TD([[makeQuery(id+"F9.imprint","IMPRINT",EDGE,{"disambiguationData":[TD([[subQ2,-1.0]])],"derivedFrom":subQ1}),-1.0]])]});}
            var Q16;
            {var subQ0=sQuery(id+"F9.wireOp",EDGE,"E72.0");var subQ1=sQuery(id+"F9.wireOp",EDGE,"E63.0");var subQ2=makeQuery(id+"F9.imprint","INTERSECT",VERTEX,{"derivedFrom":[subQ1,subQ0]});Q16=makeQuery(id+"F9.imprint","IMPRINT",FACE,{"disambiguationData":[TD([[makeQuery(id+"F9.imprint","IMPRINT",EDGE,{"disambiguationData":[TD([[subQ2,-1.0]])],"derivedFrom":subQ1}),-1.0]])]});}
            var Q17;
            {var subQ0=sQuery(id+"F9.wireOp",EDGE,"E62");var subQ1=sQuery(id+"F9.wireOp",EDGE,"E61");var subQ2=makeQuery(id+"F9.imprint","INTERSECT",VERTEX,{"derivedFrom":[subQ1,subQ0]});Q17=makeQuery(id+"F9.imprint","IMPRINT",FACE,{"disambiguationData":[TD([[makeQuery(id+"F9.imprint","IMPRINT",EDGE,{"disambiguationData":[TD([[subQ2,1.0]])],"derivedFrom":subQ1}),-1.0]])]});}
            var Q18;
            {var subQ0=sQuery(id+"F9.wireOp",EDGE,"E62");var subQ1=sQuery(id+"F9.wireOp",EDGE,"E48.left");var subQ2=makeQuery(id+"F9.imprint","INTERSECT",VERTEX,{"derivedFrom":[subQ1,subQ0]});Q18=makeQuery(id+"F9.imprint","IMPRINT",FACE,{"disambiguationData":[TD([[makeQuery(id+"F9.imprint","IMPRINT",EDGE,{"disambiguationData":[TD([[subQ2,1.0]])],"derivedFrom":subQ1}),-1.0]])]});}
            var Q19;
            {var subQ0=sQuery(id+"F9.wireOp",EDGE,"E63.0");var subQ1=sQuery(id+"F9.wireOp",EDGE,"E48.left");var subQ2=makeQuery(id+"F9.imprint","INTERSECT",VERTEX,{"derivedFrom":[subQ1,subQ0]});Q19=makeQuery(id+"F9.imprint","IMPRINT",FACE,{"disambiguationData":[TD([[makeQuery(id+"F9.imprint","IMPRINT",EDGE,{"disambiguationData":[TD([[subQ2,1.0]])],"derivedFrom":subQ1}),-1.0]])]});}
            var Q20;
            {var subQ0=sQuery(id+"F9.wireOp",EDGE,"E93.0");var subQ1=sQuery(id+"F9.wireOp",EDGE,"E68.0");var subQ2=makeQuery(id+"F9.imprint","INTERSECT",VERTEX,{"derivedFrom":[subQ1,subQ0]});Q20=makeQuery(id+"F9.imprint","IMPRINT",FACE,{"disambiguationData":[TD([[makeQuery(id+"F9.imprint","IMPRINT",EDGE,{"disambiguationData":[TD([[subQ2,1.0]])],"derivedFrom":subQ1}),1.0]])]});}
            var Q21;
            {var subQ0=sQuery(id+"F9.wireOp",EDGE,"E92");var subQ1=sQuery(id+"F9.wireOp",EDGE,"E68.0");var subQ2=makeQuery(id+"F9.imprint","INTERSECT",VERTEX,{"derivedFrom":[subQ1,subQ0]});Q21=makeQuery(id+"F9.imprint","IMPRINT",FACE,{"disambiguationData":[TD([[makeQuery(id+"F9.imprint","IMPRINT",EDGE,{"disambiguationData":[TD([[subQ2,1.0]])],"derivedFrom":subQ1}),1.0]])]});}
            var Q22;
            {var subQ0=sQuery(id+"F9.wireOp",EDGE,"E93.0");var subQ1=sQuery(id+"F9.wireOp",EDGE,"E61");var subQ2=makeQuery(id+"F9.imprint","INTERSECT",VERTEX,{"derivedFrom":[subQ1,subQ0]});Q22=makeQuery(id+"F9.imprint","IMPRINT",FACE,{"disambiguationData":[TD([[makeQuery(id+"F9.imprint","IMPRINT",EDGE,{"disambiguationData":[TD([[subQ2,-1.0]])],"derivedFrom":subQ1}),-1.0]])]});}
            var Q23;
            {var subQ0=sQuery(id+"F9.wireOp",EDGE,"E92");var subQ1=sQuery(id+"F9.wireOp",EDGE,"E48.left");var subQ2=makeQuery(id+"F9.imprint","INTERSECT",VERTEX,{"derivedFrom":[subQ1,subQ0]});Q23=makeQuery(id+"F9.imprint","IMPRINT",FACE,{"disambiguationData":[TD([[makeQuery(id+"F9.imprint","IMPRINT",EDGE,{"disambiguationData":[TD([[subQ2,1.0]])],"derivedFrom":subQ1}),-1.0]])]});}
            var Q24;
            {var subQ0=sQuery(id+"F9.wireOp",EDGE,"E93.0");var subQ1=sQuery(id+"F9.wireOp",EDGE,"E48.left");var subQ2=makeQuery(id+"F9.imprint","INTERSECT",VERTEX,{"derivedFrom":[subQ1,subQ0]});Q24=makeQuery(id+"F9.imprint","IMPRINT",FACE,{"disambiguationData":[TD([[makeQuery(id+"F9.imprint","IMPRINT",EDGE,{"disambiguationData":[TD([[subQ2,1.0]])],"derivedFrom":subQ1}),-1.0]])]});}
            var Q25;
            {var subQ0=sQuery(id+"F9.wireOp",EDGE,"E98");var subQ1=sQuery(id+"F9.wireOp",EDGE,"E69.0");var subQ2=makeQuery(id+"F9.imprint","INTERSECT",VERTEX,{"derivedFrom":[subQ1,subQ0]});Q25=makeQuery(id+"F9.imprint","IMPRINT",FACE,{"disambiguationData":[TD([[makeQuery(id+"F9.imprint","IMPRINT",EDGE,{"disambiguationData":[TD([[subQ2,1.0]])],"derivedFrom":subQ1}),-1.0]])]});}
            var Q26;
            {var subQ0=sQuery(id+"F9.wireOp",EDGE,"E97");var subQ1=sQuery(id+"F9.wireOp",EDGE,"E69.0");var subQ2=makeQuery(id+"F9.imprint","INTERSECT",VERTEX,{"derivedFrom":[subQ1,subQ0]});Q26=makeQuery(id+"F9.imprint","IMPRINT",FACE,{"disambiguationData":[TD([[makeQuery(id+"F9.imprint","IMPRINT",EDGE,{"disambiguationData":[TD([[subQ2,1.0]])],"derivedFrom":subQ1}),-1.0]])]});}
            var Q27;
            {var subQ0=sQuery(id+"F9.wireOp",EDGE,"E98");var subQ1=sQuery(id+"F9.wireOp",EDGE,"E60");var subQ2=makeQuery(id+"F9.imprint","INTERSECT",VERTEX,{"derivedFrom":[subQ1,subQ0]});Q27=makeQuery(id+"F9.imprint","IMPRINT",FACE,{"disambiguationData":[TD([[makeQuery(id+"F9.imprint","IMPRINT",EDGE,{"disambiguationData":[TD([[subQ2,-1.0]])],"derivedFrom":subQ1}),1.0]])]});}
            var Q28;
            {var subQ0=sQuery(id+"F9.wireOp",EDGE,"E99");var subQ1=sQuery(id+"F9.wireOp",EDGE,"E60");var subQ2=makeQuery(id+"F9.imprint","INTERSECT",VERTEX,{"derivedFrom":[subQ1,subQ0]});Q28=makeQuery(id+"F9.imprint","IMPRINT",FACE,{"disambiguationData":[TD([[makeQuery(id+"F9.imprint","IMPRINT",EDGE,{"disambiguationData":[TD([[subQ2,-1.0]])],"derivedFrom":subQ1}),-1.0]])]});}
            var Q29;
            {var subQ0=sQuery(id+"F9.wireOp",EDGE,"E98");var subQ1=sQuery(id+"F9.wireOp",EDGE,"E60");var subQ2=makeQuery(id+"F9.imprint","INTERSECT",VERTEX,{"derivedFrom":[subQ1,subQ0]});Q29=makeQuery(id+"F9.imprint","IMPRINT",FACE,{"disambiguationData":[TD([[makeQuery(id+"F9.imprint","IMPRINT",EDGE,{"disambiguationData":[TD([[subQ2,-1.0]])],"derivedFrom":subQ1}),-1.0]])]});}
            var Q30;
            {var subQ0=sQuery(id+"F9.wireOp",EDGE,"E110.0");var subQ1=sQuery(id+"F9.wireOp",EDGE,"E55.right");var subQ2=makeQuery(id+"F9.imprint","INTERSECT",VERTEX,{"derivedFrom":[subQ1,subQ0]});Q30=makeQuery(id+"F9.imprint","IMPRINT",FACE,{"disambiguationData":[TD([[makeQuery(id+"F9.imprint","IMPRINT",EDGE,{"disambiguationData":[TD([[subQ2,1.0]])],"derivedFrom":subQ1}),-1.0]])]});}
            var Q31;
            {var subQ0=sQuery(id+"F9.wireOp",EDGE,"E110.0");var subQ1=sQuery(id+"F9.wireOp",EDGE,"E108.0");var subQ2=makeQuery(id+"F9.imprint","INTERSECT",VERTEX,{"derivedFrom":[subQ1,subQ0]});Q31=makeQuery(id+"F9.imprint","IMPRINT",FACE,{"disambiguationData":[TD([[makeQuery(id+"F9.imprint","IMPRINT",EDGE,{"disambiguationData":[TD([[subQ2,-1.0]])],"derivedFrom":subQ1}),-1.0]])]});}
            var Q32;
            {var subQ0=sQuery(id+"F9.wireOp",EDGE,"E111.0");var subQ1=sQuery(id+"F9.wireOp",EDGE,"E108.0");var subQ2=makeQuery(id+"F9.imprint","INTERSECT",VERTEX,{"derivedFrom":[subQ1,subQ0]});Q32=makeQuery(id+"F9.imprint","IMPRINT",FACE,{"disambiguationData":[TD([[makeQuery(id+"F9.imprint","IMPRINT",EDGE,{"disambiguationData":[TD([[subQ2,-1.0]])],"derivedFrom":subQ1}),-1.0]])]});}
            var Q33;
            {var subQ0=sQuery(id+"F9.wireOp",EDGE,"E109.0");var subQ1=sQuery(id+"F9.wireOp",EDGE,"E107.0");var subQ2=makeQuery(id+"F9.imprint","INTERSECT",VERTEX,{"derivedFrom":[subQ1,subQ0]});Q33=makeQuery(id+"F9.imprint","IMPRINT",FACE,{"disambiguationData":[TD([[makeQuery(id+"F9.imprint","IMPRINT",EDGE,{"disambiguationData":[TD([[subQ2,-1.0]])],"derivedFrom":subQ1}),-1.0]])]});}
            var Q34;
            {var subQ0=sQuery(id+"F9.wireOp",EDGE,"E109.0");var subQ1=sQuery(id+"F9.wireOp",EDGE,"E55.right");var subQ2=makeQuery(id+"F9.imprint","INTERSECT",VERTEX,{"derivedFrom":[subQ1,subQ0]});Q34=makeQuery(id+"F9.imprint","IMPRINT",FACE,{"disambiguationData":[TD([[makeQuery(id+"F9.imprint","IMPRINT",EDGE,{"disambiguationData":[TD([[subQ2,-1.0]])],"derivedFrom":subQ1}),-1.0]])]});}
            extrude(context, id + "F12", {"entities" : qUnion([Q0, Q1, Q2, Q3, Q4, Q5, Q6, Q7, Q8, Q9, Q10, Q11, Q12, Q13, Q14, Q15, Q16, Q17, Q18, Q19, Q20, Q21, Q22, Q23, Q24, Q25, Q26, Q27, Q28, Q29, Q30, Q31, Q32, Q33, Q34]), "depth" : 400 * mm, "offsetDistance" : 25 * mm});
        }
        {
            var Q0;
            Q0=makeQuery(id+"F12.opExtrude","SWEPT_FACE",FACE,{"disambiguationData":[OSD([sQuery(id+"F9.wireOp",EDGE,"E98")])]});
            var sketch = newSketch(context, id + "F13", { "sketchPlane" : qUnion([Q0])});
            skLineSegment(sketch, "E113.bottom", {"start": v(964, 0) * mm, "end": v(575.18, 0) * mm});
            skLineSegment(sketch, "E113.top", {"start": v(964, 15) * mm, "end": v(575.18, 15) * mm});
            skLineSegment(sketch, "E113.left", {"start": v(964, 0) * mm, "end": v(964, 15) * mm});
            skLineSegment(sketch, "E113.right", {"start": v(575.18, 0) * mm, "end": v(575.18, 15) * mm});
            skLineSegment(sketch, "E114.bottom", {"start": v(521.18, 0) * mm, "end": v(36, 0) * mm});
            skLineSegment(sketch, "E114.top", {"start": v(521.18, 15) * mm, "end": v(36, 15) * mm});
            skLineSegment(sketch, "E114.left", {"start": v(521.18, 0) * mm, "end": v(521.18, 15) * mm});
            skLineSegment(sketch, "E114.right", {"start": v(36, 0) * mm, "end": v(36, 15) * mm});
            skSolve(sketch);
        }
        {
            var Q0;
            {var subQ0=sQuery(id+"F13.wireOp",EDGE,"E113.bottom");var subQ1=sQuery(id+"F9.wireOp",EDGE,"E98");var subQ2=makeQuery(id+"F12.opExtrude","SWEPT_EDGE",EDGE,{"disambiguationData":[OSD([sQuery(id+"F9.wireOp",EDGE,"E60"),subQ1])]});var subQ3=makeQuery(id+"F13.imprint","INTERSECT",VERTEX,{"derivedFrom":[subQ2,subQ0]});var subQ4=makeQuery(id+"F12.opExtrude","SWEPT_EDGE",EDGE,{"disambiguationData":[OSD([sQuery(id+"F9.wireOp",EDGE,"E73.0"),subQ1])]});var subQ5=makeQuery(id+"F13.imprint","INTERSECT",VERTEX,{"derivedFrom":[subQ4,subQ0]});Q0=makeQuery(id+"F13.imprint","IMPRINT",FACE,{"disambiguationData":[TD([[makeQuery(id+"F13.imprint","IMPRINT",EDGE,{"disambiguationData":[TD([[subQ3,1.0],[subQ5,-1.0]])],"derivedFrom":subQ0}),1.0]])]});}
            var Q1;
            Q1=makeQuery(id+"F13.imprint","IMPRINT",FACE,{"disambiguationData":[TD([[makeQuery(id+"F13.imprint","IMPRINT",EDGE,{"derivedFrom":sQuery(id+"F13.wireOp",EDGE,"E114.bottom")}),-1.0]])]});
            var Q2;
            {var subQ3=sQuery(id+"F13.wireOp",EDGE,"E113.left");Q2=makeQuery(id+"F13.imprint","IMPRINT",FACE,{"disambiguationData":[TD([[makeQuery(id+"F13.imprint","IMPRINT",EDGE,{"derivedFrom":subQ3}),1.0]])]});}
            var Q3;
            {var subQ3=sQuery(id+"F13.wireOp",EDGE,"E113.right");Q3=makeQuery(id+"F13.imprint","IMPRINT",FACE,{"disambiguationData":[TD([[makeQuery(id+"F13.imprint","IMPRINT",EDGE,{"derivedFrom":subQ3}),-1.0]])]});}
            var Q4;
            {var subQ0=sQuery(id+"F9.wireOp",EDGE,"E94.0");Q4=makeQuery(id+"F12.opExtrude","SWEPT_FACE",FACE,{"disambiguationData":[OSD([subQ0]),TDD([makeQuery(id+"F9.imprint","IMPRINT",EDGE,{"disambiguationData":[TD([[makeQuery(id+"F9.imprint","INTERSECT",VERTEX,{"derivedFrom":[sQuery(id+"F9.wireOp",EDGE,"E68.0"),subQ0]}),-1.0]])],"derivedFrom":subQ0})])]});}
            var Q5;
            Q5=makeQuery(id+"F12.opExtrude","SWEPT_FACE",FACE,{"disambiguationData":[OSD([sQuery(id+"F9.wireOp",EDGE,"E92")])]});
            extrude(context, id + "F14", {"entities" : qUnion([Q0, Q1, Q2, Q3]), "endBound" : BoundingType.UP_TO_SURFACE, "depth" : 25 * mm, "endBoundEntityFace" : qUnion([Q4]), "offsetDistance" : 25 * mm, "hasSecondDirection" : true, "secondDirectionBound" : SecondDirectionBoundingType.UP_TO_SURFACE, "secondDirectionOppositeDirection" : true, "secondDirectionDepth" : 25 * mm, "secondDirectionBoundEntityFace" : qUnion([Q5])});
        }
        {
            var Q0;
            Q0=makeQuery(id+"F14.opExtrude","SWEPT_BODY",BODY,{"disambiguationData":[OSD([sQuery(id+"F13.wireOp",EDGE,"E113.bottom"),sQuery(id+"F13.wireOp",EDGE,"E113.top"),sQuery(id+"F13.wireOp",EDGE,"E113.left"),sQuery(id+"F13.wireOp",EDGE,"E113.right")])]});
            var Q1;
            Q1=makeQuery(id+"F14.opExtrude","SWEPT_BODY",BODY,{"disambiguationData":[OSD([sQuery(id+"F13.wireOp",EDGE,"E114.bottom"),sQuery(id+"F13.wireOp",EDGE,"E114.top"),sQuery(id+"F13.wireOp",EDGE,"E114.left"),sQuery(id+"F13.wireOp",EDGE,"E114.right")])]});
            var Q2;
            Q2=makeQuery(id+"F12.opExtrude","SWEPT_BODY",BODY,{"disambiguationData":[OSD([sQuery(id+"F9.wireOp",EDGE,"E60"),sQuery(id+"F9.wireOp",EDGE,"E66"),sQuery(id+"F9.wireOp",EDGE,"E69.0"),sQuery(id+"F9.wireOp",EDGE,"E73.0"),sQuery(id+"F9.wireOp",EDGE,"E97"),sQuery(id+"F9.wireOp",EDGE,"E98"),sQuery(id+"F9.wireOp",EDGE,"E99")])]});
            var Q3;
            Q3=makeQuery(id+"F12.opExtrude","SWEPT_BODY",BODY,{"disambiguationData":[OSD([sQuery(id+"F9.wireOp",EDGE,"E48.left"),sQuery(id+"F9.wireOp",EDGE,"E61"),sQuery(id+"F9.wireOp",EDGE,"E68.0"),sQuery(id+"F9.wireOp",EDGE,"E72.0"),sQuery(id+"F9.wireOp",EDGE,"E92"),sQuery(id+"F9.wireOp",EDGE,"E93.0"),sQuery(id+"F9.wireOp",EDGE,"E94.0")])]});
            booleanBodies(context, id + "F15", {"operationType" : BooleanOperationType.SUBTRACTION, "tools" : qUnion([Q0, Q1]), "targets" : qUnion([Q2, Q3]), "keepTools" : true});
        }
        {
            var Q0;
            Q0=makeQuery(id+"F10.opExtrude","SWEPT_FACE",FACE,{"disambiguationData":[OSD([sQuery(id+"F9.wireOp",EDGE,"E105")])]});
            var sketch = newSketch(context, id + "F16", { "sketchPlane" : qUnion([Q0])});
            skLineSegment(sketch, "E115.bottom", {"start": v(18, 0) * mm, "end": v(660.4, 0) * mm});
            skLineSegment(sketch, "E115.top", {"start": v(18, 12) * mm, "end": v(660.4, 12) * mm});
            skLineSegment(sketch, "E115.left", {"start": v(18, 0) * mm, "end": v(18, 12) * mm});
            skLineSegment(sketch, "E115.right", {"start": v(660.4, 0) * mm, "end": v(660.4, 12) * mm});
            skSolve(sketch);
        }
        {
            var Q0;
            Q0=makeQuery(id+"F16.imprint","IMPRINT",FACE,{"disambiguationData":[TD([[makeQuery(id+"F16.imprint","IMPRINT",EDGE,{"derivedFrom":sQuery(id+"F16.wireOp",EDGE,"E115.bottom")}),1.0]])]});
            var Q1;
            Q1=makeQuery(id+"F11.opExtrude","SWEPT_FACE",FACE,{"disambiguationData":[OSD([sQuery(id+"F9.wireOp",EDGE,"E103.top")])]});
            extrude(context, id + "F17", {"entities" : qUnion([Q0]), "endBound" : BoundingType.UP_TO_SURFACE, "depth" : 25 * mm, "endBoundEntityFace" : qUnion([Q1]), "offsetDistance" : 25 * mm});
        }
        {
            var Q0;
            Q0=makeQuery(id+"F2.opExtrude","SWEPT_FACE",FACE,{"disambiguationData":[OSD([sQuery(id+"F0.wireOp",EDGE,"E5.0")])]});
            var sketch = newSketch(context, id + "F18", { "sketchPlane" : qUnion([Q0])});
            skArc(sketch, "E116", {"start": v(70.49, 607.38) * mm, "mid": v(65.5, 672) * mm, "end": v(60.51, 607.38) * mm});
            skArc(sketch, "E117", {"start": v(70.49, 607.38) * mm, "mid": v(65.5, 612) * mm, "end": v(60.51, 607.38) * mm});
            skArc(sketch, "E118.0", {"start": v(71.96, 609.7) * mm, "mid": v(65.5, 670) * mm, "end": v(59.04, 609.7) * mm});
            skArc(sketch, "E119.0", {"start": v(71.96, 609.7) * mm, "mid": v(65.5, 614) * mm, "end": v(59.04, 609.7) * mm});
            skCircle(sketch, "E120", {"center": v(65.5, 639.5) * mm, "radius": 32.5 * mm});
            skSolve(sketch);
        }
        {
            var Q0;
            {var subQ0=sQuery(id+"F18.wireOp",EDGE,"E117");Q0=makeQuery(id+"F18.imprint","IMPRINT",FACE,{"disambiguationData":[TD([[makeQuery(id+"F18.imprint","IMPRINT",EDGE,{"derivedFrom":subQ0}),-1.0]])]});}
            var Q1;
            {var subQ0=sQuery(id+"F18.wireOp",EDGE,"E117");Q1=makeQuery(id+"F18.imprint","IMPRINT",FACE,{"disambiguationData":[TD([[makeQuery(id+"F18.imprint","IMPRINT",EDGE,{"derivedFrom":subQ0}),1.0]])]});}
            var Q2;
            Q2=makeQuery(id+"F2.opExtrude","SWEPT_FACE",FACE,{"disambiguationData":[OSD([sQuery(id+"F0.wireOp",EDGE,"E0.top")])]});
            extrude(context, id + "F19", {"entities" : qUnion([Q0, Q1]), "operationType" : NewBodyOperationType.REMOVE, "endBound" : BoundingType.UP_TO_SURFACE, "oppositeDirection" : true, "depth" : 25 * mm, "endBoundEntityFace" : qUnion([Q2]), "offsetDistance" : 25 * mm});
        }
        {
            var Q0;
            {var subQ0=sQuery(id+"F18.wireOp",EDGE,"E117");Q0=makeQuery(id+"F18.imprint","IMPRINT",FACE,{"disambiguationData":[TD([[makeQuery(id+"F18.imprint","IMPRINT",EDGE,{"derivedFrom":subQ0}),-1.0]])]});}
            var Q1;
            {var subQ1=sQuery(id+"F0.wireOp",EDGE,"E1.0");var subQ3=sQuery(id+"F0.wireOp",EDGE,"E0.top");Q1=makeQuery(id+"F19.boolean.opBoolean","SPLIT",FACE,{"disambiguationData":[TD([makeQuery(id+"F2.opExtrude","SWEPT_FACE",FACE,{"disambiguationData":[OSD([subQ1])]})])],"derivedFrom":makeQuery(id+"F2.opExtrude","SWEPT_FACE",FACE,{"disambiguationData":[OSD([subQ3])]})});}
            extrude(context, id + "F20", {"entities" : qUnion([Q0]), "endBound" : BoundingType.UP_TO_SURFACE, "oppositeDirection" : true, "depth" : 25 * mm, "endBoundEntityFace" : qUnion([Q1]), "offsetDistance" : 25 * mm});
        }
    });
